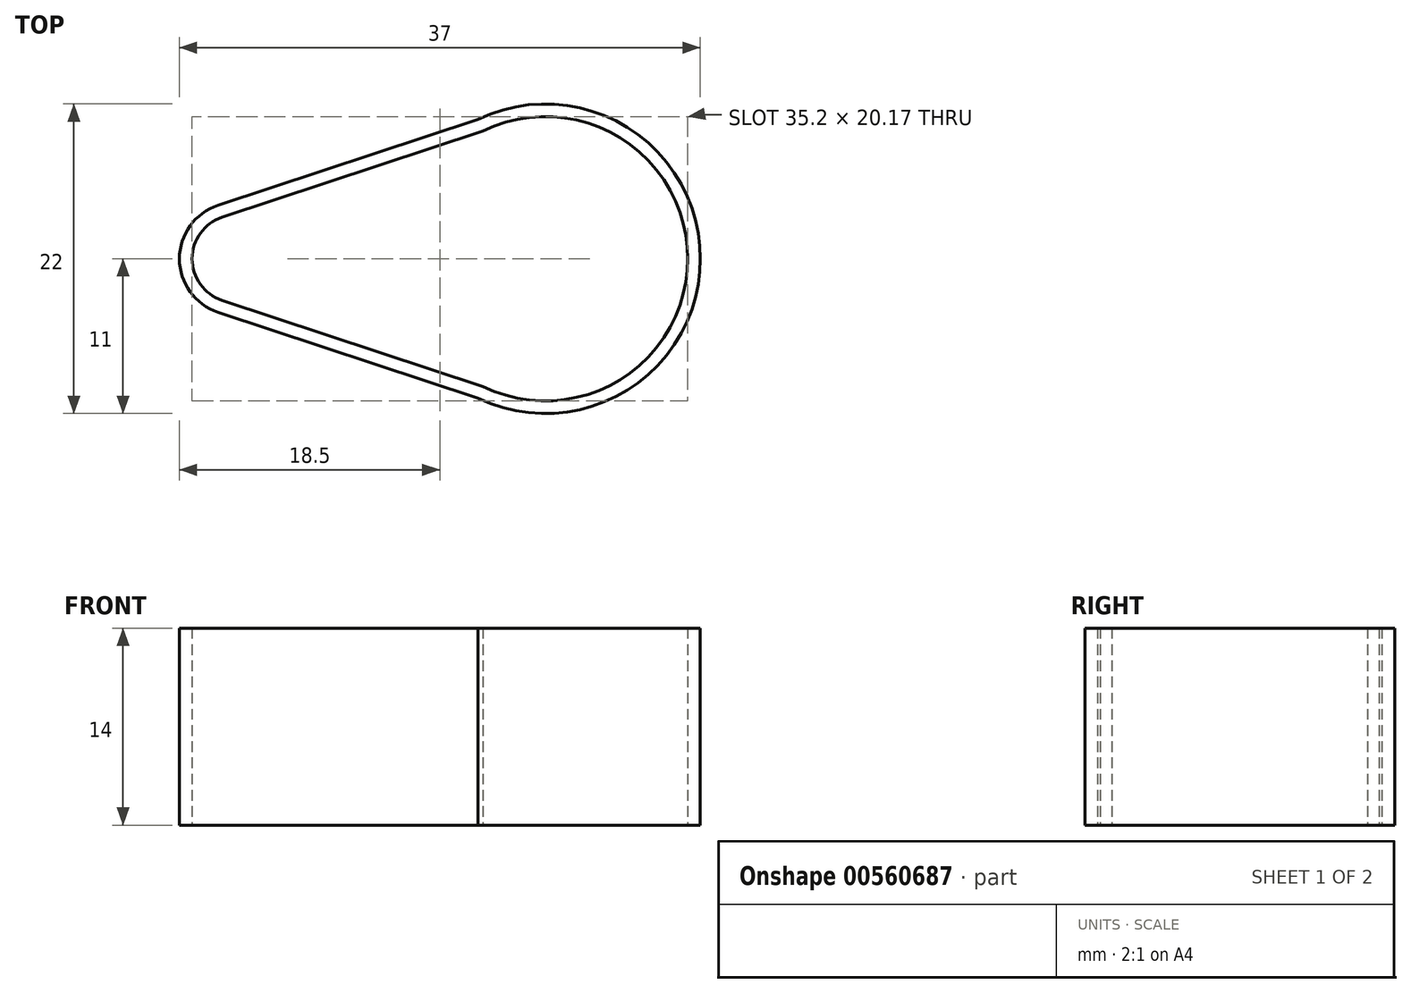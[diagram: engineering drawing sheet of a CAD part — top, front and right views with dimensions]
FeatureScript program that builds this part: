
annotation { "Feature Type Name" : "Feature", "Feature Type Description" : "" }
export const myFeature = defineFeature(function(context is Context, id is Id, definition is map)
    precondition{}
    {
        {
            var Q0;
            Q0=qCreatedBy(makeId("Top.planeOp"),FACE);
            var sketch = newSketch(context, id + "F0", { "sketchPlane" : qUnion([Q0])});
            skArc(sketch, "E0", {"start": v(-4.79, -9.9) * mm, "mid": v(11, 0) * mm, "end": v(-4.79, 9.9) * mm});
            skArc(sketch, "E1", {"start": v(-23.26, 3.8) * mm, "mid": v(-26, 0) * mm, "end": v(-23.26, -3.8) * mm});
            skLineSegment(sketch, "E2", {"start": v(-4.79, 9.9) * mm, "end": v(-23.26, 3.8) * mm});
            skLineSegment(sketch, "E3", {"start": v(-23.26, -3.8) * mm, "end": v(-4.79, -9.9) * mm});
            skLineSegment(sketch, "E4.0", {"start": v(-0.85, -5.94) * mm, "end": v(-0.49, -6.06) * mm});
            skPoint(sketch, "E5.orphan", {"position": v(-2.06, -10.8) * mm});
            skPoint(sketch, "E6.orphan", {"position": v(-2.06, 10.8) * mm});
            skSolve(sketch);
        }
        {
            var Q0;
            Q0=makeQuery(id+"F0.imprint","IMPRINT",FACE,{"disambiguationData":[TD([[makeQuery(id+"F0.imprint","IMPRINT",EDGE,{"derivedFrom":sQuery(id+"F0.wireOp",EDGE,"E0")}),1.0]])]});
            var sketch = newSketch(context, id + "F1", { "sketchPlane" : qUnion([Q0])});
            skLineSegment(sketch, "E7.0", {"start": v(-4.45, 9.07) * mm, "end": v(-22.97, 2.94) * mm});
            skArc(sketch, "E7.1", {"start": v(-4.45, -9.07) * mm, "mid": v(10.1, 0) * mm, "end": v(-4.45, 9.07) * mm});
            skLineSegment(sketch, "E7.2", {"start": v(-22.97, -2.94) * mm, "end": v(-4.45, -9.07) * mm});
            skArc(sketch, "E7.3", {"start": v(-22.97, 2.94) * mm, "mid": v(-25.1, 0) * mm, "end": v(-22.97, -2.94) * mm});
            skSolve(sketch);
        }
        {
            var Q0;
            Q0 = qSketchRegion(id + "F0", true);
            extrude(context, id + "F2", {"entities" : qUnion([Q0]), "depth" : 14 * mm, "offsetDistance" : 25 * mm});
        }
        {
            var Q0;
            Q0 = qSketchRegion(id + "F1", true);
            extrude(context, id + "F3", {"entities" : qUnion([Q0]), "operationType" : NewBodyOperationType.REMOVE, "depth" : 14 * mm, "offsetDistance" : 25 * mm});
        }
    });
